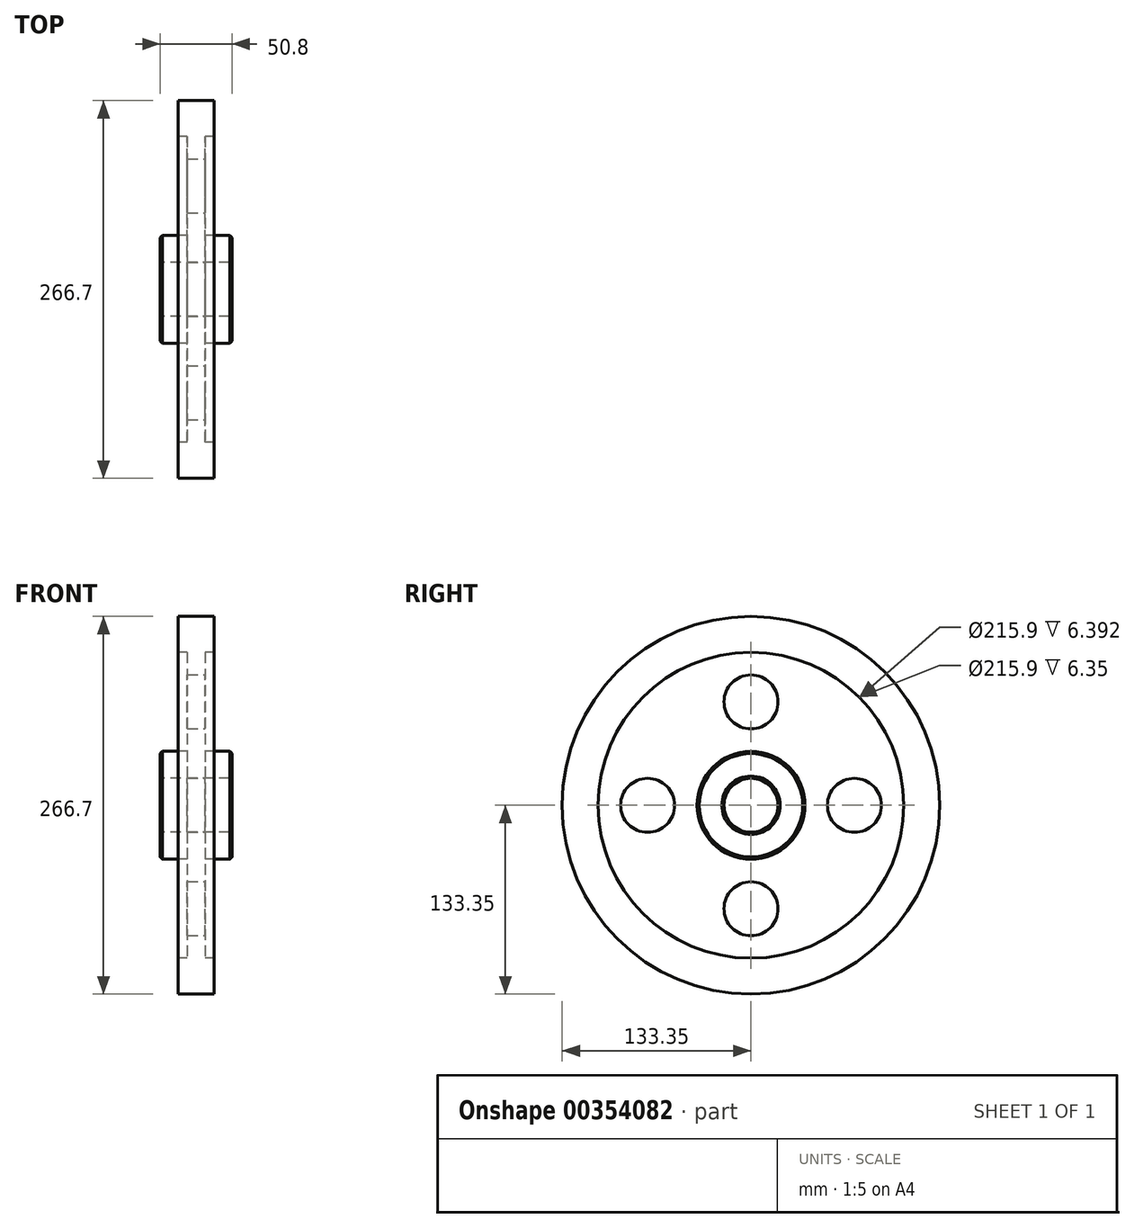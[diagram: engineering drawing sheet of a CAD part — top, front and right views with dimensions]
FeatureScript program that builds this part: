
annotation { "Feature Type Name" : "Feature", "Feature Type Description" : "" }
export const myFeature = defineFeature(function(context is Context, id is Id, definition is map)
    precondition{}
    {
        {
            var Q0;
            Q0=qCreatedBy(makeId("Front.planeOp"),FACE);
            var sketch = newSketch(context, id + "F0", { "sketchPlane" : qUnion([Q0])});
            skLineSegment(sketch, "E0", {"start": v(0, 0) * mm, "end": v(76.23, 0) * mm, "construction": true});
            skLineSegment(sketch, "E1.0", {"start": v(0, 19.05) * mm, "end": v(25.4, 19.05) * mm});
            skLineSegment(sketch, "E2.0", {"start": v(6.35, 38.1) * mm, "end": v(25.4, 38.1) * mm});
            skLineSegment(sketch, "E3.0", {"start": v(6.35, 107.95) * mm, "end": v(12.7, 107.95) * mm});
            skLineSegment(sketch, "E4.0", {"start": v(0, 133.35) * mm, "end": v(6.35, 133.35) * mm});
            skLineSegment(sketch, "E5", {"start": v(0, 133.35) * mm, "end": v(0, 107.95) * mm, "construction": true});
            skLineSegment(sketch, "E6.0", {"start": v(25.4, 38.1) * mm, "end": v(25.4, 19.05) * mm});
            skLineSegment(sketch, "E7.0", {"start": v(12.7, 120.65) * mm, "end": v(12.7, 107.95) * mm});
            skLineSegment(sketch, "E8.0", {"start": v(6.35, 107.95) * mm, "end": v(6.35, 38.1) * mm});
            skLineSegment(sketch, "E9", {"start": v(6.35, 133.35) * mm, "end": v(12.74, 133.35) * mm});
            skLineSegment(sketch, "E10", {"start": v(12.74, 133.35) * mm, "end": v(12.7, 120.65) * mm});
            skLineSegment(sketch, "E11.trimOffspring", {"start": v(0, 38.1) * mm, "end": v(0, 0) * mm, "construction": true});
            skLineSegment(sketch, "E12", {"start": v(0, 107.95) * mm, "end": v(0, 38.1) * mm});
            skPoint(sketch, "E13.endSnap0", {"position": v(12.7, 114.3) * mm});
            skPoint(sketch, "E13.end.orphan", {"position": v(12.7, 28.87) * mm});
            skLineSegment(sketch, "E14.MirrorCS", {"start": v(-6.35, 107.95) * mm, "end": v(-6.35, 38.1) * mm});
            skLineSegment(sketch, "E15.MirrorCS", {"start": v(-6.35, 38.1) * mm, "end": v(-25.4, 38.1) * mm});
            skLineSegment(sketch, "E16.MirrorCS", {"start": v(-25.4, 38.1) * mm, "end": v(-25.4, 19.05) * mm});
            skLineSegment(sketch, "E17.MirrorCS", {"start": v(0, 19.05) * mm, "end": v(-25.4, 19.05) * mm});
            skLineSegment(sketch, "E18.MirrorCS", {"start": v(-12.74, 133.35) * mm, "end": v(-12.7, 120.65) * mm});
            skPoint(sketch, "E19.MirrorP", {"position": v(-12.7, 114.3) * mm});
            skLineSegment(sketch, "E20.bottom", {"start": v(12.7, 107.95) * mm, "end": v(-12.74, 107.95) * mm});
            skLineSegment(sketch, "E20.top", {"start": v(12.7, 133.35) * mm, "end": v(-12.74, 133.35) * mm});
            skLineSegment(sketch, "E20.left", {"start": v(12.7, 107.95) * mm, "end": v(12.7, 133.35) * mm});
            skLineSegment(sketch, "E20.right", {"start": v(-12.74, 107.95) * mm, "end": v(-12.74, 133.35) * mm});
            skSolve(sketch);
        }
        {
            var Q0;
            {var subQ2=sQuery(id+"F0.wireOp",EDGE,"E20.right");Q0=makeQuery(id+"F0.imprint","IMPRINT",FACE,{"disambiguationData":[TD([[makeQuery(id+"F0.imprint","IMPRINT",EDGE,{"derivedFrom":subQ2}),-1.0]])]});}
            var Q1;
            Q1=makeQuery(id+"F0.imprint","IMPRINT",FACE,{"disambiguationData":[TD([[makeQuery(id+"F0.imprint","IMPRINT",EDGE,{"derivedFrom":sQuery(id+"F0.wireOp",EDGE,"E1.0")}),1.0]])]});
            var Q2;
            Q2=sQuery(id+"F0.wireOp",EDGE,"E0");
            revolve(context, id + "F1", {"entities" : qUnion([Q0, Q1]), "axis" : qUnion([Q2]), "revolveType" : RevolveType.FULL});
        }
        {
            var Q0;
            Q0=makeQuery(id+"F1.opRevolve","SWEPT_FACE",FACE,{"disambiguationData":[OSD([sQuery(id+"F0.wireOp",EDGE,"E8.0")])]});
            var sketch = newSketch(context, id + "F2", { "sketchPlane" : qUnion([Q0])});
            skLineSegment(sketch, "E21", {"start": v(0, 0) * mm, "end": v(0, 73.03) * mm});
            skCircle(sketch, "E22", {"center": v(0, 73.03) * mm, "radius": 19.05 * mm});
            skLineSegment(sketch, "E23", {"start": v(0, 0) * mm, "end": v(-73.03, 0) * mm});
            skCircle(sketch, "E24", {"center": v(-73.03, 0) * mm, "radius": 19.05 * mm});
            skLineSegment(sketch, "E25", {"start": v(0, 0) * mm, "end": v(0, -73.03) * mm});
            skCircle(sketch, "E26", {"center": v(0, -73.03) * mm, "radius": 19.05 * mm});
            skLineSegment(sketch, "E27", {"start": v(0, 0) * mm, "end": v(73.03, 0) * mm});
            skCircle(sketch, "E28", {"center": v(73.03, 0) * mm, "radius": 19.05 * mm});
            skSolve(sketch);
        }
        {
            var Q0;
            Q0=makeQuery(id+"F2.imprint","IMPRINT",FACE,{"disambiguationData":[TD([[makeQuery(id+"F2.imprint","IMPRINT",EDGE,{"derivedFrom":sQuery(id+"F2.wireOp",EDGE,"E24")}),1.0]])]});
            var Q1;
            Q1=makeQuery(id+"F2.imprint","IMPRINT",FACE,{"disambiguationData":[TD([[makeQuery(id+"F2.imprint","IMPRINT",EDGE,{"derivedFrom":sQuery(id+"F2.wireOp",EDGE,"E22")}),1.0]])]});
            var Q2;
            Q2=makeQuery(id+"F2.imprint","IMPRINT",FACE,{"disambiguationData":[TD([[makeQuery(id+"F2.imprint","IMPRINT",EDGE,{"derivedFrom":sQuery(id+"F2.wireOp",EDGE,"E28")}),1.0]])]});
            var Q3;
            Q3=makeQuery(id+"F2.imprint","IMPRINT",FACE,{"disambiguationData":[TD([[makeQuery(id+"F2.imprint","IMPRINT",EDGE,{"derivedFrom":sQuery(id+"F2.wireOp",EDGE,"E26")}),1.0]])]});
            extrude(context, id + "F3", {"entities" : qUnion([Q0, Q1, Q2, Q3]), "operationType" : NewBodyOperationType.REMOVE, "oppositeDirection" : true, "depth" : 25.4 * mm});
        }
        {
            var Q0;
            Q0=makeQuery(id+"F1.opRevolve","SWEPT_EDGE",EDGE,{"disambiguationData":[OSD([sQuery(id+"F0.wireOp",EDGE,"E2.0"),sQuery(id+"F0.wireOp",EDGE,"E6.0")])]});
            var Q1;
            Q1=makeQuery(id+"F1.opRevolve","SWEPT_EDGE",EDGE,{"disambiguationData":[OSD([sQuery(id+"F0.wireOp",EDGE,"E1.0"),sQuery(id+"F0.wireOp",EDGE,"E6.0")])]});
            chamfer(context, id + "F4", {"entities" : qUnion([Q0, Q1]), "width" : 1.59 * mm, "tangentPropagation" : true});
        }
        {
            var Q0;
            Q0=makeQuery(id+"F1.opRevolve","SWEPT_EDGE",EDGE,{"disambiguationData":[OSD([sQuery(id+"F0.wireOp",EDGE,"E15.MirrorCS"),sQuery(id+"F0.wireOp",EDGE,"E16.MirrorCS")])]});
            var Q1;
            Q1=makeQuery(id+"F1.opRevolve","SWEPT_EDGE",EDGE,{"disambiguationData":[OSD([sQuery(id+"F0.wireOp",EDGE,"E16.MirrorCS"),sQuery(id+"F0.wireOp",EDGE,"E17.MirrorCS")])]});
            chamfer(context, id + "F5", {"entities" : qUnion([Q0, Q1]), "width" : 1.59 * mm, "tangentPropagation" : true});
        }
    });
